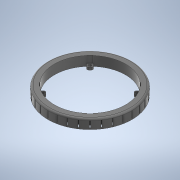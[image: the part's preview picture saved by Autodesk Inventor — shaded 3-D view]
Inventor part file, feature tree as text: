
AUTODESK INVENTOR PART (.ipt)
format: ipt  version: 2020 (Build 240168000, 168)  size: 915,968 bytes
history: native  units: mm
features: extrude x7, projected_geometry x7, sketch x6, pattern_circular x4, fillet x3, other x1
ambient origin geometry x8: Origin, YZ Plane, XZ Plane, XY Plane, X Axis, Y Axis, Z Axis, Center Point
bodies: Body1 (feature_tree)
feature tree (28):
  other  "Твердое тело1"
  sketch  "Эскиз1"
  extrude  "Выдавливание1"  Depth=88.0mm
  extrude  "Выдавливание2"  Depth=5.3mm
  pattern_circular  "Круговой массив1"  [2 undecoded]
  extrude  "Выдавливание3"  Depth=5.1mm
  fillet  "Сопряжение1"  Radius=98.0mm
  extrude  "Выдавливание4"  Depth=84.0mm
  pattern_circular  "Круговой массив2"  [2 undecoded]
  fillet  "Сопряжение2"  Radius=98.0mm
  extrude  "Выдавливание5"  Depth=84.0mm
  pattern_circular  "Круговой массив3"  [2 undecoded]
  extrude  "Выдавливание6"  Depth=10.0mm TaperAngle=0.0deg
  fillet  "Сопряжение3"  Radius=320.0mm
  sketch  "Эскиз6"
  extrude  "Выдавливание7"  Depth=2.0mm
  pattern_circular  "Круговой массив4"  [2 undecoded]
  sketch  "Эскиз2"
  sketch  "Эскиз3"
  projected_geometry  "Спроецированная петля1"
  sketch  "Эскиз4"
  projected_geometry  "Спроецированная петля2"
  sketch  "Эскиз5"
  projected_geometry  "Спроецированная петля3"
  projected_geometry  "Спроецированная петля4"
  projected_geometry  "Спроецированная петля5"
  projected_geometry  "Спроецированная петля6"
  projected_geometry  "Спроецированная петля7"
note: 8 required parameter values undecoded (feature->parameter linkage not recoverable at this tier; creation-order binding heuristic only, values carry confidence <= 0.55)
